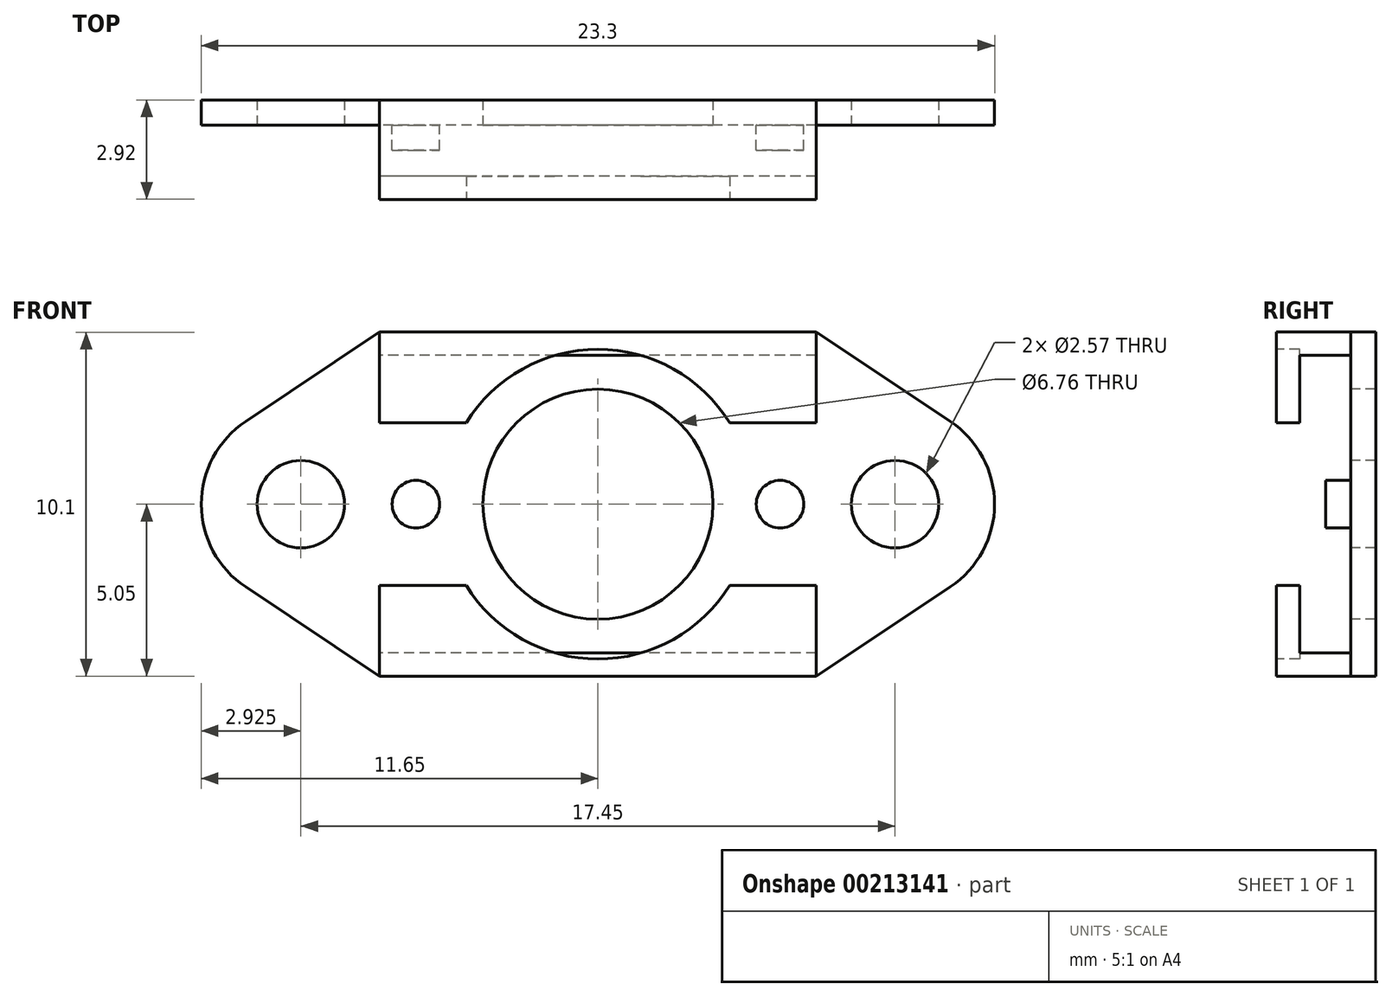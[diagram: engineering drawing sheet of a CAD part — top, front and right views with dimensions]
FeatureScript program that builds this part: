
annotation { "Feature Type Name" : "Feature", "Feature Type Description" : "" }
export const myFeature = defineFeature(function(context is Context, id is Id, definition is map)
    precondition{}
    {
        {
            var Q0;
            Q0=qCreatedBy(makeId("Front.planeOp"),FACE);
            var sketch = newSketch(context, id + "F0", { "sketchPlane" : qUnion([Q0])});
            skLineSegment(sketch, "E0.bottom", {"start": v(11.65, -5.05) * mm, "end": v(-11.65, -5.05) * mm});
            skLineSegment(sketch, "E0.top", {"start": v(11.65, 5.05) * mm, "end": v(-11.65, 5.05) * mm});
            skLineSegment(sketch, "E0.left", {"start": v(11.65, -5.05) * mm, "end": v(11.65, 5.05) * mm});
            skLineSegment(sketch, "E0.right", {"start": v(-11.65, -5.05) * mm, "end": v(-11.65, 5.05) * mm});
            skPoint(sketch, "E0.middle", {"position": v(0, 0) * mm});
            skSolve(sketch);
        }
        {
            var Q0;
            Q0=makeQuery(id+"F0.imprint","IMPRINT",FACE,{"disambiguationData":[TD([[makeQuery(id+"F0.imprint","IMPRINT",EDGE,{"derivedFrom":sQuery(id+"F0.wireOp",EDGE,"E0.bottom")}),-1.0]])]});
            extrude(context, id + "F1", {"entities" : qUnion([Q0]), "depth" : 0.74 * mm});
        }
        {
            var Q0;
            Q0=makeQuery(id+"F1.opExtrude","CAP_FACE",FACE,{"disambiguationData":[OSD([sQuery(id+"F0.wireOp",EDGE,"E0.bottom"),sQuery(id+"F0.wireOp",EDGE,"E0.top"),sQuery(id+"F0.wireOp",EDGE,"E0.left"),sQuery(id+"F0.wireOp",EDGE,"E0.right")])],"isStart":false});
            var sketch = newSketch(context, id + "F2", { "sketchPlane" : qUnion([Q0])});
            skArc(sketch, "E1", {"start": v(10.35, -2.43) * mm, "mid": v(11.65, 0) * mm, "end": v(10.35, 2.43) * mm});
            skArc(sketch, "E2", {"start": v(-10.35, 2.43) * mm, "mid": v(-11.65, 0) * mm, "end": v(-10.35, -2.43) * mm});
            skLineSegment(sketch, "E3", {"start": v(0, 5.05) * mm, "end": v(-6.41, 5.05) * mm});
            skLineSegment(sketch, "E4", {"start": v(0, 5.05) * mm, "end": v(6.41, 5.05) * mm});
            skLineSegment(sketch, "E5", {"start": v(-6.41, 5.05) * mm, "end": v(-6.41, -5.05) * mm});
            skLineSegment(sketch, "E6", {"start": v(6.41, 5.05) * mm, "end": v(6.41, -5.05) * mm});
            skLineSegment(sketch, "E7", {"start": v(-6.41, -5.05) * mm, "end": v(6.41, -5.05) * mm});
            skLineSegment(sketch, "E8", {"start": v(-6.41, 5.05) * mm, "end": v(-10.35, 2.43) * mm});
            skLineSegment(sketch, "E9", {"start": v(-6.41, -5.05) * mm, "end": v(-10.35, -2.43) * mm});
            skLineSegment(sketch, "E10", {"start": v(6.41, -5.05) * mm, "end": v(10.35, -2.43) * mm});
            skLineSegment(sketch, "E11", {"start": v(6.41, 5.05) * mm, "end": v(10.35, 2.43) * mm});
            skLineSegment(sketch, "E12", {"start": v(-6.41, 5.05) * mm, "end": v(-11.65, 5.05) * mm});
            skLineSegment(sketch, "E13", {"start": v(-11.65, 5.05) * mm, "end": v(-11.65, -5.05) * mm});
            skLineSegment(sketch, "E14", {"start": v(-11.65, -5.05) * mm, "end": v(-6.41, -5.05) * mm});
            skLineSegment(sketch, "E15", {"start": v(6.41, 5.05) * mm, "end": v(11.65, 5.05) * mm});
            skLineSegment(sketch, "E16", {"start": v(11.65, 5.05) * mm, "end": v(11.65, -5.05) * mm});
            skLineSegment(sketch, "E17", {"start": v(11.65, -5.05) * mm, "end": v(6.41, -5.05) * mm});
            skSolve(sketch);
        }
        {
            var Q0;
            {var subQ0=sQuery(id+"F2.wireOp",EDGE,"E8");Q0=makeQuery(id+"F2.imprint","IMPRINT",FACE,{"disambiguationData":[TD([[makeQuery(id+"F2.imprint","IMPRINT",EDGE,{"derivedFrom":subQ0}),-1.0]])]});}
            var Q1;
            {var subQ0=sQuery(id+"F2.wireOp",EDGE,"E9");Q1=makeQuery(id+"F2.imprint","IMPRINT",FACE,{"disambiguationData":[TD([[makeQuery(id+"F2.imprint","IMPRINT",EDGE,{"derivedFrom":subQ0}),1.0]])]});}
            var Q2;
            {var subQ0=sQuery(id+"F2.wireOp",EDGE,"E10");Q2=makeQuery(id+"F2.imprint","IMPRINT",FACE,{"disambiguationData":[TD([[makeQuery(id+"F2.imprint","IMPRINT",EDGE,{"derivedFrom":subQ0}),-1.0]])]});}
            var Q3;
            {var subQ0=sQuery(id+"F2.wireOp",EDGE,"E11");Q3=makeQuery(id+"F2.imprint","IMPRINT",FACE,{"disambiguationData":[TD([[makeQuery(id+"F2.imprint","IMPRINT",EDGE,{"derivedFrom":subQ0}),1.0]])]});}
            extrude(context, id + "F3", {"entities" : qUnion([Q0, Q1, Q2, Q3]), "operationType" : NewBodyOperationType.REMOVE, "oppositeDirection" : true, "depth" : 25.4 * mm});
        }
        {
            var Q0;
            Q0=makeQuery(id+"F1.opExtrude","CAP_FACE",FACE,{"disambiguationData":[OSD([sQuery(id+"F0.wireOp",EDGE,"E0.bottom"),sQuery(id+"F0.wireOp",EDGE,"E0.top"),sQuery(id+"F0.wireOp",EDGE,"E0.left"),sQuery(id+"F0.wireOp",EDGE,"E0.right")])],"isStart":false});
            var sketch = newSketch(context, id + "F4", { "sketchPlane" : qUnion([Q0])});
            skCircle(sketch, "E18", {"center": v(8.72, 0) * mm, "radius": 1.28 * mm});
            skCircle(sketch, "E19", {"center": v(-8.72, 0) * mm, "radius": 1.28 * mm});
            skCircle(sketch, "E20", {"center": v(0, 0) * mm, "radius": 3.38 * mm});
            skSolve(sketch);
        }
        {
            var Q0;
            Q0=makeQuery(id+"F4.imprint","IMPRINT",FACE,{"disambiguationData":[TD([[makeQuery(id+"F4.imprint","IMPRINT",EDGE,{"derivedFrom":sQuery(id+"F4.wireOp",EDGE,"E19")}),1.0]])]});
            var Q1;
            Q1=makeQuery(id+"F4.imprint","IMPRINT",FACE,{"disambiguationData":[TD([[makeQuery(id+"F4.imprint","IMPRINT",EDGE,{"derivedFrom":sQuery(id+"F4.wireOp",EDGE,"E20")}),1.0]])]});
            var Q2;
            Q2=makeQuery(id+"F4.imprint","IMPRINT",FACE,{"disambiguationData":[TD([[makeQuery(id+"F4.imprint","IMPRINT",EDGE,{"derivedFrom":sQuery(id+"F4.wireOp",EDGE,"E18")}),1.0]])]});
            extrude(context, id + "F5", {"entities" : qUnion([Q0, Q1, Q2]), "operationType" : NewBodyOperationType.REMOVE, "endBound" : BoundingType.THROUGH_ALL, "oppositeDirection" : true, "depth" : 25.4 * mm});
        }
        {
            var Q0;
            Q0=makeQuery(id+"F1.opExtrude","CAP_FACE",FACE,{"disambiguationData":[OSD([sQuery(id+"F0.wireOp",EDGE,"E0.bottom"),sQuery(id+"F0.wireOp",EDGE,"E0.top"),sQuery(id+"F0.wireOp",EDGE,"E0.left"),sQuery(id+"F0.wireOp",EDGE,"E0.right")])],"isStart":false});
            var sketch = newSketch(context, id + "F6", { "sketchPlane" : qUnion([Q0])});
            skLineSegment(sketch, "E21", {"start": v(-11.65, 0) * mm, "end": v(-5.35, 0) * mm});
            skPoint(sketch, "E21.endSnap0", {"position": v(-11.65, 0) * mm});
            skLineSegment(sketch, "E22", {"start": v(11.65, 0) * mm, "end": v(5.35, 0) * mm});
            skCircle(sketch, "E23", {"center": v(-5.35, 0) * mm, "radius": 0.7 * mm});
            skCircle(sketch, "E24", {"center": v(5.35, 0) * mm, "radius": 0.7 * mm});
            skSolve(sketch);
        }
        {
            var Q0;
            Q0=makeQuery(id+"F6.imprint","IMPRINT",FACE,{"disambiguationData":[TD([[makeQuery(id+"F6.imprint","IMPRINT",EDGE,{"derivedFrom":sQuery(id+"F6.wireOp",EDGE,"E23")}),1.0]])]});
            var Q1;
            Q1=makeQuery(id+"F6.imprint","IMPRINT",FACE,{"disambiguationData":[TD([[makeQuery(id+"F6.imprint","IMPRINT",EDGE,{"derivedFrom":sQuery(id+"F6.wireOp",EDGE,"E24")}),1.0]])]});
            extrude(context, id + "F7", {"entities" : qUnion([Q0, Q1]), "operationType" : NewBodyOperationType.ADD, "depth" : 0.74 * mm});
        }
        {
            var Q0;
            Q0=makeQuery(id+"F1.opExtrude","CAP_FACE",FACE,{"disambiguationData":[OSD([sQuery(id+"F0.wireOp",EDGE,"E0.bottom"),sQuery(id+"F0.wireOp",EDGE,"E0.top"),sQuery(id+"F0.wireOp",EDGE,"E0.left"),sQuery(id+"F0.wireOp",EDGE,"E0.right")])],"isStart":false});
            var sketch = newSketch(context, id + "F8", { "sketchPlane" : qUnion([Q0])});
            skLineSegment(sketch, "E25", {"start": v(-6.41, -5.05) * mm, "end": v(-6.41, -2.39) * mm});
            skLineSegment(sketch, "E26", {"start": v(6.41, -5.05) * mm, "end": v(6.41, -2.39) * mm});
            skLineSegment(sketch, "E27", {"start": v(-6.41, -2.39) * mm, "end": v(6.41, -2.39) * mm});
            skLineSegment(sketch, "E28", {"start": v(-6.41, 5.05) * mm, "end": v(-6.41, 2.39) * mm});
            skLineSegment(sketch, "E29", {"start": v(6.41, 5.05) * mm, "end": v(6.41, 2.39) * mm});
            skLineSegment(sketch, "E30", {"start": v(-6.41, 2.39) * mm, "end": v(6.41, 2.39) * mm});
            skSolve(sketch);
        }
        {
            var Q0;
            {var subQ4=sQuery(id+"F8.wireOp",EDGE,"E28");Q0=makeQuery(id+"F8.imprint","IMPRINT",FACE,{"disambiguationData":[TD([[makeQuery(id+"F8.imprint","IMPRINT",EDGE,{"derivedFrom":subQ4}),1.0]])]});}
            var Q1;
            {var subQ5=sQuery(id+"F8.wireOp",EDGE,"E25");Q1=makeQuery(id+"F8.imprint","IMPRINT",FACE,{"disambiguationData":[TD([[makeQuery(id+"F8.imprint","IMPRINT",EDGE,{"derivedFrom":subQ5}),-1.0]])]});}
            extrude(context, id + "F9", {"entities" : qUnion([Q0, Q1]), "operationType" : NewBodyOperationType.ADD, "depth" : 2.18 * mm});
        }
        {
            var Q0;
            Q0=makeQuery(id+"F9.opExtrude","SWEPT_FACE",FACE,{"disambiguationData":[OSD([sQuery(id+"F8.wireOp",EDGE,"E28")])]});
            var sketch = newSketch(context, id + "F10", { "sketchPlane" : qUnion([Q0])});
            skLineSegment(sketch, "E31", {"start": v(0.74, 5.05) * mm, "end": v(0.74, 4.37) * mm});
            skLineSegment(sketch, "E32", {"start": v(0.74, 4.37) * mm, "end": v(2.24, 4.37) * mm});
            skLineSegment(sketch, "E33", {"start": v(2.24, 2.39) * mm, "end": v(2.24, 4.37) * mm});
            skPoint(sketch, "E34.start.orphan", {"position": v(2.92, 3.72) * mm});
            skSolve(sketch);
        }
        {
            var Q0;
            {var subQ0=sQuery(id+"F10.wireOp",EDGE,"E32");Q0=makeQuery(id+"F10.imprint","IMPRINT",FACE,{"disambiguationData":[TD([[makeQuery(id+"F10.imprint","IMPRINT",EDGE,{"derivedFrom":subQ0}),-1.0]])]});}
            extrude(context, id + "F11", {"entities" : qUnion([Q0]), "operationType" : NewBodyOperationType.REMOVE, "endBound" : BoundingType.THROUGH_ALL, "oppositeDirection" : true, "depth" : 25.4 * mm});
        }
        {
            var Q0;
            Q0=makeQuery(id+"F9.opExtrude","SWEPT_FACE",FACE,{"disambiguationData":[OSD([sQuery(id+"F8.wireOp",EDGE,"E25")])]});
            var sketch = newSketch(context, id + "F12", { "sketchPlane" : qUnion([Q0])});
            skLineSegment(sketch, "E35", {"start": v(2.92, -2.39) * mm, "end": v(2.24, -2.39) * mm});
            skLineSegment(sketch, "E36", {"start": v(0.74, -5.05) * mm, "end": v(0.74, -4.37) * mm});
            skLineSegment(sketch, "E37", {"start": v(0.74, -4.37) * mm, "end": v(2.24, -4.37) * mm});
            skLineSegment(sketch, "E38", {"start": v(2.24, -2.39) * mm, "end": v(2.24, -4.37) * mm});
            skSolve(sketch);
        }
        {
            var Q0;
            {var subQ0=sQuery(id+"F12.wireOp",EDGE,"E37");Q0=makeQuery(id+"F12.imprint","IMPRINT",FACE,{"disambiguationData":[TD([[makeQuery(id+"F12.imprint","IMPRINT",EDGE,{"derivedFrom":subQ0}),1.0]])]});}
            extrude(context, id + "F13", {"entities" : qUnion([Q0]), "operationType" : NewBodyOperationType.REMOVE, "endBound" : BoundingType.THROUGH_ALL, "oppositeDirection" : true, "depth" : 25.4 * mm});
        }
        {
            var Q0;
            Q0=makeQuery(id+"F9.opExtrude","CAP_FACE",FACE,{"disambiguationData":[OSD([sQuery(id+"F0.wireOp",EDGE,"E0.top"),sQuery(id+"F4.wireOp",EDGE,"E20"),sQuery(id+"F8.wireOp",EDGE,"E28"),sQuery(id+"F8.wireOp",EDGE,"E29"),sQuery(id+"F8.wireOp",EDGE,"E30")])],"isStart":false});
            var sketch = newSketch(context, id + "F14", { "sketchPlane" : qUnion([Q0])});
            skArc(sketch, "E39", {"start": v(3.87, 2.39) * mm, "mid": v(0, 4.55) * mm, "end": v(-3.87, 2.39) * mm});
            skLineSegment(sketch, "E40", {"start": v(-6.41, 2.39) * mm, "end": v(-3.87, 2.39) * mm});
            skLineSegment(sketch, "E41.trimOffspring", {"start": v(3.87, 2.39) * mm, "end": v(6.41, 2.39) * mm});
            skSolve(sketch);
        }
        {
            var Q0;
            {var subQ0=sQuery(id+"F14.wireOp",EDGE,"E39");Q0=makeQuery(id+"F14.imprint","IMPRINT",FACE,{"disambiguationData":[TD([[makeQuery(id+"F14.imprint","IMPRINT",EDGE,{"derivedFrom":subQ0}),1.0]])]});}
            extrude(context, id + "F15", {"entities" : qUnion([Q0]), "operationType" : NewBodyOperationType.REMOVE, "oppositeDirection" : true, "depth" : 0.69 * mm});
        }
        {
            var Q0;
            Q0=makeQuery(id+"F9.opExtrude","CAP_FACE",FACE,{"disambiguationData":[OSD([sQuery(id+"F0.wireOp",EDGE,"E0.bottom"),sQuery(id+"F4.wireOp",EDGE,"E20"),sQuery(id+"F8.wireOp",EDGE,"E25"),sQuery(id+"F8.wireOp",EDGE,"E26"),sQuery(id+"F8.wireOp",EDGE,"E27")])],"isStart":false});
            var sketch = newSketch(context, id + "F16", { "sketchPlane" : qUnion([Q0])});
            skArc(sketch, "E42", {"start": v(-3.87, -2.39) * mm, "mid": v(0, -4.55) * mm, "end": v(3.87, -2.39) * mm});
            skLineSegment(sketch, "E43", {"start": v(-6.41, -2.39) * mm, "end": v(-3.87, -2.39) * mm});
            skLineSegment(sketch, "E44.trimOffspring", {"start": v(3.87, -2.39) * mm, "end": v(6.41, -2.39) * mm});
            skSolve(sketch);
        }
        {
            var Q0;
            {var subQ0=sQuery(id+"F16.wireOp",EDGE,"E42");Q0=makeQuery(id+"F16.imprint","IMPRINT",FACE,{"disambiguationData":[TD([[makeQuery(id+"F16.imprint","IMPRINT",EDGE,{"derivedFrom":subQ0}),1.0]])]});}
            extrude(context, id + "F17", {"entities" : qUnion([Q0]), "operationType" : NewBodyOperationType.REMOVE, "oppositeDirection" : true, "depth" : 0.69 * mm});
        }
    });
